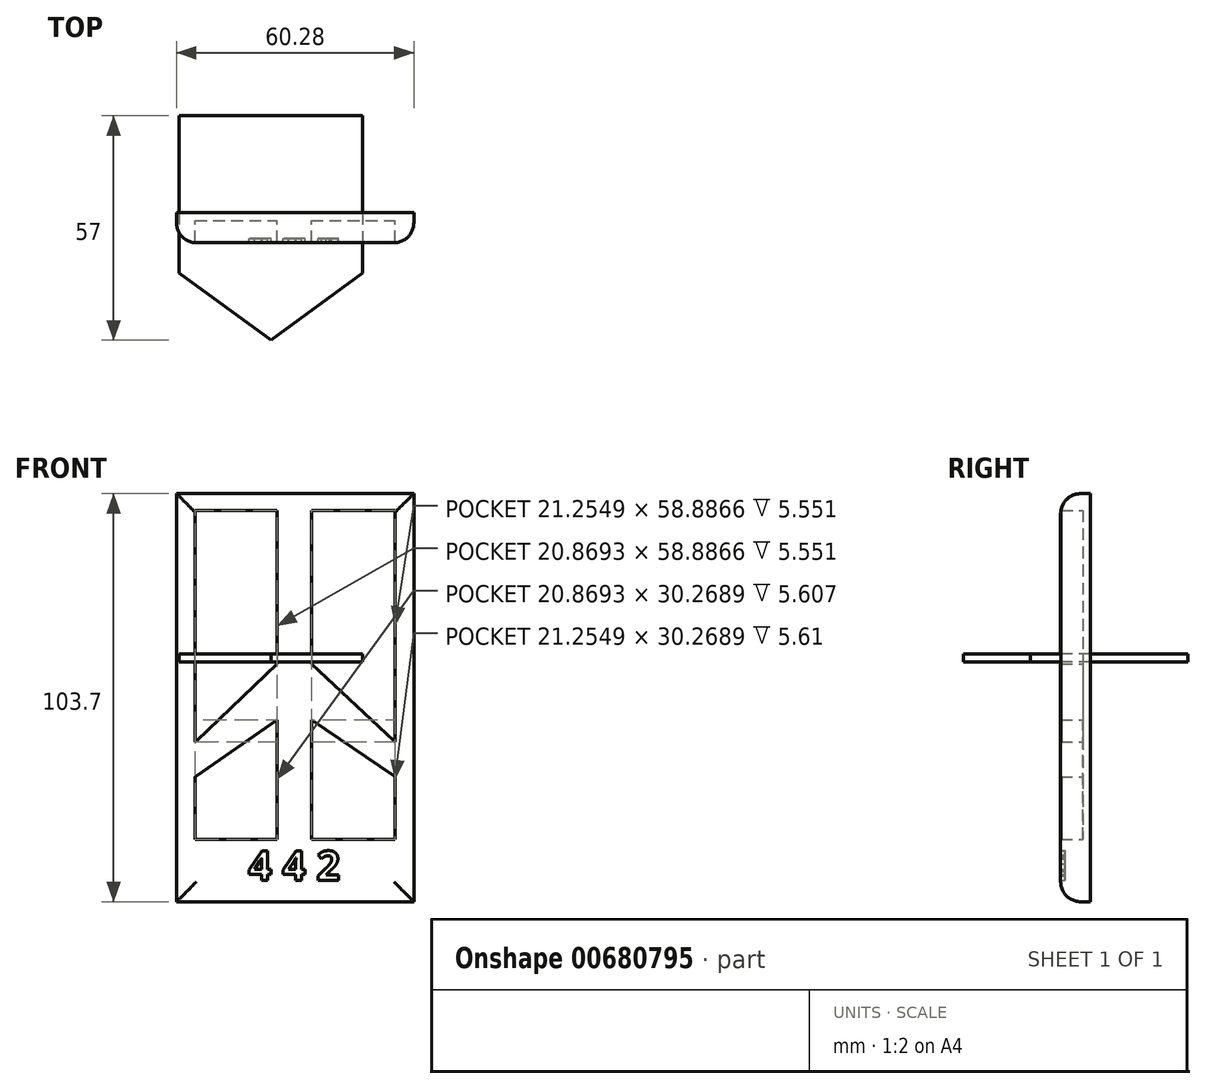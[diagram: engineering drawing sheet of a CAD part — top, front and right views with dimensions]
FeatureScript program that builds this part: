
annotation { "Feature Type Name" : "Feature", "Feature Type Description" : "" }
export const myFeature = defineFeature(function(context is Context, id is Id, definition is map)
    precondition{}
    {
        {
            var Q0;
            Q0=qCreatedBy(makeId("Front.planeOp"),FACE);
            var sketch = newSketch(context, id + "F0", { "sketchPlane" : qUnion([Q0])});
            skLineSegment(sketch, "E0.bottom", {"start": v(-25.4, 38.55) * mm, "end": v(25.4, 38.55) * mm});
            skLineSegment(sketch, "E0.top", {"start": v(-25.4, -56.7) * mm, "end": v(25.4, -56.7) * mm});
            skLineSegment(sketch, "E0.left", {"start": v(-25.4, 38.55) * mm, "end": v(-25.4, -56.7) * mm});
            skLineSegment(sketch, "E0.right", {"start": v(25.4, 38.55) * mm, "end": v(25.4, -56.7) * mm});
            skPoint(sketch, "E1", {"position": v(-25.4, -45.02) * mm});
            skPoint(sketch, "E2", {"position": v(25.4, -45.02) * mm});
            skLineSegment(sketch, "E3", {"start": v(-25.4, -45.02) * mm, "end": v(25.4, -45.02) * mm});
            skPoint(sketch, "E4", {"position": v(4.15, -45.02) * mm});
            skPoint(sketch, "E5", {"position": v(-4.53, -45.02) * mm});
            skPoint(sketch, "E6", {"position": v(4.15, 38.55) * mm});
            skPoint(sketch, "E7", {"position": v(-4.53, 38.55) * mm});
            skLineSegment(sketch, "E8", {"start": v(4.15, -45.02) * mm, "end": v(4.15, -14.75) * mm});
            skLineSegment(sketch, "E9", {"start": v(-4.53, -45.02) * mm, "end": v(-4.53, -14.75) * mm});
            skLineSegment(sketch, "E10", {"start": v(4.15, 38.55) * mm, "end": v(4.15, -0.48) * mm});
            skLineSegment(sketch, "E11", {"start": v(-4.53, 38.55) * mm, "end": v(-4.53, -0.48) * mm});
            skLineSegment(sketch, "E12", {"start": v(4.15, -14.75) * mm, "end": v(25.4, -29.2) * mm});
            skLineSegment(sketch, "E13", {"start": v(4.15, -0.48) * mm, "end": v(25.4, -20.34) * mm});
            skLineSegment(sketch, "E14", {"start": v(-4.53, -0.48) * mm, "end": v(-25.4, -20.34) * mm});
            skLineSegment(sketch, "E15", {"start": v(-4.53, -14.75) * mm, "end": v(-25.4, -29.2) * mm});
            skPoint(sketch, "E16", {"position": v(-30.12, 42.8) * mm});
            skPoint(sketch, "E17", {"position": v(30.16, -60.9) * mm});
            skLineSegment(sketch, "E18.bottom", {"start": v(-30.12, 42.8) * mm, "end": v(30.16, 42.8) * mm});
            skLineSegment(sketch, "E18.top", {"start": v(-30.12, -60.9) * mm, "end": v(30.16, -60.9) * mm});
            skLineSegment(sketch, "E18.left", {"start": v(-30.12, 42.8) * mm, "end": v(-30.12, -60.9) * mm});
            skLineSegment(sketch, "E18.right", {"start": v(30.16, 42.8) * mm, "end": v(30.16, -60.9) * mm});
            skText(sketch, "E19", { "text": "4 4 2", "fontName": "OpenSans-Bold.ttf"});
            skLineSegment(sketch, "E20", {"start": v(-25.4, -47.38) * mm, "end": v(25.4, -47.38) * mm});
            const initialGuessF0  = {"E19": [-0.01189, -0.05547, 1, 0, 0.00752]};
            skSetInitialGuess(sketch, initialGuessF0);
            skSolve(sketch);
        }
        {
            var Q0;
            {var subQ4=sQuery(id+"F0.wireOp",EDGE,"E8");Q0=makeQuery(id+"F0.imprint","IMPRINT",FACE,{"disambiguationData":[TD([[makeQuery(id+"F0.imprint","IMPRINT",EDGE,{"derivedFrom":subQ4}),1.0]])]});}
            var Q1;
            {var subQ7=sQuery(id+"F0.wireOp",EDGE,"E20");Q1=makeQuery(id+"F0.imprint","IMPRINT",FACE,{"disambiguationData":[TD([[makeQuery(id+"F0.imprint","IMPRINT",EDGE,{"derivedFrom":subQ7}),1.0]])]});}
            var Q2;
            {var subQ5=sQuery(id+"F0.wireOp",EDGE,"E0.top");Q2=makeQuery(id+"F0.imprint","IMPRINT",FACE,{"disambiguationData":[TD([[makeQuery(id+"F0.imprint","IMPRINT",EDGE,{"derivedFrom":subQ5}),-1.0]])]});}
            extrude(context, id + "F1", {"entities" : qUnion([Q0, Q1, Q2]), "depth" : 7.62 * mm, "offsetDistance" : 25.4 * mm});
        }
        {
            var Q0;
            {var subQ3=sQuery(id+"F0.wireOp",EDGE,"E10");Q0=makeQuery(id+"F0.imprint","IMPRINT",FACE,{"disambiguationData":[TD([[makeQuery(id+"F0.imprint","IMPRINT",EDGE,{"derivedFrom":subQ3}),1.0]])]});}
            var Q1;
            {var subQ3=sQuery(id+"F0.wireOp",EDGE,"E11");Q1=makeQuery(id+"F0.imprint","IMPRINT",FACE,{"disambiguationData":[TD([[makeQuery(id+"F0.imprint","IMPRINT",EDGE,{"derivedFrom":subQ3}),-1.0]])]});}
            var Q2;
            {var subQ4=sQuery(id+"F0.wireOp",EDGE,"E9");Q2=makeQuery(id+"F0.imprint","IMPRINT",FACE,{"disambiguationData":[TD([[makeQuery(id+"F0.imprint","IMPRINT",EDGE,{"derivedFrom":subQ4}),1.0]])]});}
            var Q3;
            {var subQ4=sQuery(id+"F0.wireOp",EDGE,"E8");Q3=makeQuery(id+"F0.imprint","IMPRINT",FACE,{"disambiguationData":[TD([[makeQuery(id+"F0.imprint","IMPRINT",EDGE,{"derivedFrom":subQ4}),-1.0]])]});}
            extrude(context, id + "F2", {"entities" : qUnion([Q0, Q1, Q2, Q3]), "operationType" : NewBodyOperationType.ADD, "depth" : 2 * mm, "offsetDistance" : 25.4 * mm});
        }
        {
            var Q0;
            {var subQ1=sQuery(id+"F0.wireOp",EDGE,"E0.top");Q0=makeQuery(id+"F0.imprint","IMPRINT",FACE,{"disambiguationData":[TD([[makeQuery(id+"F0.imprint","IMPRINT",EDGE,{"derivedFrom":subQ1}),1.0]])]});}
            extrude(context, id + "F3", {"entities" : qUnion([Q0]), "operationType" : NewBodyOperationType.ADD, "depth" : 7.62 * mm, "offsetDistance" : 25.4 * mm});
        }
        {
            var Q0;
            Q0=makeQuery(id+"F0.imprint","IMPRINT",FACE,{"disambiguationData":[TD([[makeQuery(id+"F0.imprint","IMPRINT",EDGE,{"derivedFrom":sQuery(id+"F0.wireOp",EDGE,"E19.sketch_text.stroke-0")}),-1.0]])]});
            var Q1;
            Q1=makeQuery(id+"F0.imprint","IMPRINT",FACE,{"disambiguationData":[TD([[makeQuery(id+"F0.imprint","IMPRINT",EDGE,{"derivedFrom":sQuery(id+"F0.wireOp",EDGE,"E19.sketch_text.stroke-18")}),-1.0]])]});
            var Q2;
            Q2=makeQuery(id+"F0.imprint","IMPRINT",FACE,{"disambiguationData":[TD([[makeQuery(id+"F0.imprint","IMPRINT",EDGE,{"derivedFrom":sQuery(id+"F0.wireOp",EDGE,"E19.sketch_text.stroke-36")}),-1.0]])]});
            extrude(context, id + "F4", {"entities" : qUnion([Q0, Q1, Q2]), "operationType" : NewBodyOperationType.ADD, "depth" : 6.5 * mm, "offsetDistance" : 25.4 * mm});
        }
        {
            var Q0;
            Q0=makeQuery(id+"F1.opExtrude","CAP_EDGE",EDGE,{"disambiguationData":[OSD([sQuery(id+"F0.wireOp",EDGE,"E18.right")])],"isStart":false});
            var Q1;
            Q1=makeQuery(id+"F1.opExtrude","CAP_EDGE",EDGE,{"disambiguationData":[OSD([sQuery(id+"F0.wireOp",EDGE,"E18.top")])],"isStart":false});
            var Q2;
            Q2=makeQuery(id+"F1.opExtrude","CAP_EDGE",EDGE,{"disambiguationData":[OSD([sQuery(id+"F0.wireOp",EDGE,"E18.left")])],"isStart":false});
            var Q3;
            Q3=makeQuery(id+"F1.opExtrude","CAP_EDGE",EDGE,{"disambiguationData":[OSD([sQuery(id+"F0.wireOp",EDGE,"E18.bottom")])],"isStart":false});
            fillet(context, id + "F5", {"entities" : qUnion([Q0, Q1, Q2, Q3]), "radius" : 5.08 * mm, "tangentPropagation" : true, "allowEdgeOverflow" : false});
        }
        {
            var Q0;
            Q0=makeQuery(id+"F0.imprint","IMPRINT",FACE,{"disambiguationData":[TD([[makeQuery(id+"F0.imprint","IMPRINT",EDGE,{"derivedFrom":sQuery(id+"F0.wireOp",EDGE,"E19.sketch_text.stroke-29")}),1.0]])]});
            var Q1;
            Q1=makeQuery(id+"F0.imprint","IMPRINT",FACE,{"disambiguationData":[TD([[makeQuery(id+"F0.imprint","IMPRINT",EDGE,{"derivedFrom":sQuery(id+"F0.wireOp",EDGE,"E19.sketch_text.stroke-11")}),1.0]])]});
            extrude(context, id + "F6", {"entities" : qUnion([Q0, Q1]), "operationType" : NewBodyOperationType.ADD, "depth" : 7.62 * mm, "offsetDistance" : 25.4 * mm});
        }
        {
            var Q0;
            Q0=qCreatedBy(makeId("Top.planeOp"),FACE);
            var sketch = newSketch(context, id + "F7", { "sketchPlane" : qUnion([Q0])});
            skLineSegment(sketch, "E21.bottom", {"start": v(-29.48, 24.65) * mm, "end": v(17.17, 24.65) * mm});
            skLineSegment(sketch, "E21.top", {"start": v(-29.48, -15.35) * mm, "end": v(17.17, -15.35) * mm});
            skLineSegment(sketch, "E21.left", {"start": v(-29.48, 24.65) * mm, "end": v(-29.48, -15.35) * mm});
            skLineSegment(sketch, "E21.right", {"start": v(17.17, 24.65) * mm, "end": v(17.17, -15.35) * mm});
            skPoint(sketch, "E22", {"position": v(-6.16, -15.35) * mm});
            skPoint(sketch, "E23", {"position": v(-6.16, -32.35) * mm});
            skLineSegment(sketch, "E24", {"start": v(-29.48, -15.35) * mm, "end": v(-6.16, -32.35) * mm});
            skLineSegment(sketch, "E25", {"start": v(17.17, -15.35) * mm, "end": v(-6.16, -32.35) * mm});
            skSolve(sketch);
        }
        {
            var Q0;
            Q0=makeQuery(id+"F7.imprint","IMPRINT",FACE,{"disambiguationData":[TD([[makeQuery(id+"F7.imprint","IMPRINT",EDGE,{"derivedFrom":sQuery(id+"F7.wireOp",EDGE,"E21.bottom")}),-1.0]])]});
            var Q1;
            Q1=makeQuery(id+"F7.imprint","IMPRINT",FACE,{"disambiguationData":[TD([[makeQuery(id+"F7.imprint","IMPRINT",EDGE,{"derivedFrom":sQuery(id+"F7.wireOp",EDGE,"E21.top")}),-1.0]])]});
            extrude(context, id + "F8", {"entities" : qUnion([Q0, Q1]), "depth" : 2.1 * mm, "offsetDistance" : 25.4 * mm});
        }
    });
